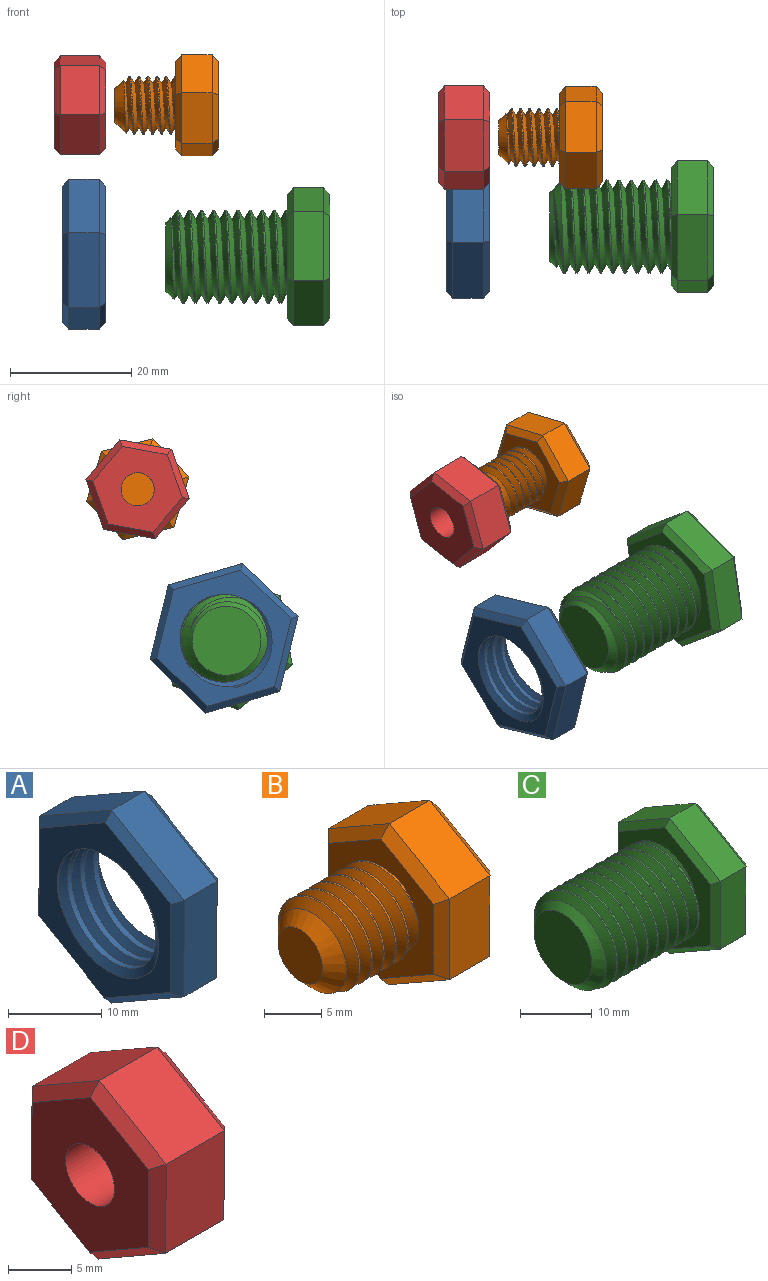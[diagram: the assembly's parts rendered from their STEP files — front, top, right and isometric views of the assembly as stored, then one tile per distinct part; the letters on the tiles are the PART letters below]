
ASSEMBLY  parts=4 mates=2
PART A: 23 faces, bbox 9.3x22.7x26 mm
  f0: cylinder r=7.24mm len=14.48mm, axis (1,0,0), area 111.6mm2, adj f7,f8,f21,f22
  f1: plane 10.98x6.38mm, normal (0,-0.5,0.86), area 63.5mm2, adj f2,f6,f14,f18
  f2: plane 12.7x5mm, normal (0,-1,0), area 63.5mm2, adj f1,f3,f12,f16
  f3: plane 11.02x6.32mm, normal (0,-0.5,-0.87), area 63.5mm2, adj f2,f4,f10,f15
  f4: plane 10.98x6.38mm, normal (0,0.5,-0.86), area 63.5mm2, adj f3,f5,f9,f17
  f5: plane 12.7x5mm, normal (0,1,0), area 63.5mm2, adj f4,f6,f11,f19
  f6: plane 11.02x6.32mm, normal (0,0.5,0.87), area 63.5mm2, adj f1,f5,f13,f20
  f7: plane 23.73x20.67mm, normal (-1,0,0), area 164.4mm2, adj f0,f9,f10,f11,f12,f13,f14,f21
  f8: plane 23.73x20.67mm, normal (1,0,0), area 164.4mm2, adj f0,f15,f16,f17,f18,f19,f20,f21
  f9: plane 10.99x6.96mm, normal (-0.71,0.36,-0.61), area 17.1mm2, adj f4,f7,f10,f11
  f10: plane 11.02x6.9mm, normal (-0.71,-0.35,-0.61), area 17.1mm2, adj f3,f7,f9,f12
  f11: plane 12.7x1.03mm, normal (-0.71,0.71,0), area 17.1mm2, adj f5,f7,f9,f13
  f12: plane 12.7x1.03mm, normal (-0.71,-0.71,0), area 17.1mm2, adj f2,f7,f10,f14
  f13: plane 11.02x6.9mm, normal (-0.71,0.35,0.61), area 17.1mm2, adj f6,f7,f11,f14
  f14: plane 10.99x6.96mm, normal (-0.71,-0.36,0.61), area 17.1mm2, adj f1,f7,f12,f13
  f15: plane 11.02x6.9mm, normal (0.71,-0.35,-0.61), area 17.1mm2, adj f3,f8,f16,f17
  f16: plane 12.7x1.03mm, normal (0.71,-0.71,0), area 17.1mm2, adj f2,f8,f15,f18
  f17: plane 10.99x6.96mm, normal (0.71,0.36,-0.61), area 17.1mm2, adj f4,f8,f15,f19
  f18: plane 10.99x6.96mm, normal (0.71,-0.36,0.61), area 17.1mm2, adj f1,f8,f16,f20
  f19: plane 12.7x1.03mm, normal (0.71,0.71,0), area 17.1mm2, adj f5,f8,f17,f20
  f20: plane 11.02x6.9mm, normal (0.71,0.35,0.61), area 17.1mm2, adj f6,f8,f18,f19
  f21: bspline ~19.31x16.73mm, area 223mm2, adj f0,f7,f8,f22
  f22: bspline ~19.31x16.73mm, area 223mm2, adj f0,f7,f8,f21
PART B: 25 faces, bbox 17.8x15.9x18.1 mm
  f0: cylinder r=4.75mm len=9.5mm, axis (1,0,0), area 28.1mm2, adj f1,f2,f4,f12
  f1: bspline ~10.97x9.91mm, area 196.7mm2, adj f0,f2,f4,f12
  f2: bspline ~10.97x10.66mm, area 196.6mm2, adj f0,f1,f4,f12
  f3: plane 5.5x5.5mm, normal (-1,0,0), area 23.8mm2, adj f4
  f4: cone r=4.75mm half-angle=45deg, axis (1,0,0), area 47.4mm2, adj f0,f1,f2,f3
  f5: plane 7.48x5mm, normal (0,-0.5,0.86), area 43.3mm2, adj f6,f10,f18,f22
  f6: plane 8.66x5mm, normal (0,-1,0), area 43.3mm2, adj f5,f7,f16,f20
  f7: plane 7.52x5mm, normal (0,-0.5,-0.87), area 43.3mm2, adj f6,f8,f14,f19
  f8: plane 7.48x5mm, normal (0,0.5,-0.86), area 43.3mm2, adj f7,f9,f13,f21
  f9: plane 8.66x5mm, normal (0,1,0), area 43.3mm2, adj f8,f10,f15,f23
  f10: plane 7.52x5mm, normal (0,0.5,0.87), area 43.3mm2, adj f5,f9,f17,f24
  f11: plane 15.01x13.03mm, normal (1,0,0), area 146.4mm2, adj f13,f14,f15,f16,f17,f18
  f12: plane 15.83x13.85mm, normal (-1,0,0), area 89.2mm2, adj f0,f1,f2,f19,f20,f21,f22,f23
  f13: plane 7.49x4.93mm, normal (0.71,0.36,-0.61), area 11.4mm2, adj f8,f11,f14,f15
  f14: plane 7.52x4.88mm, normal (0.71,-0.35,-0.61), area 11.4mm2, adj f7,f11,f13,f16
  f15: plane 8.66x1.03mm, normal (0.71,0.71,0), area 11.4mm2, adj f9,f11,f13,f17
  f16: plane 8.66x1.03mm, normal (0.71,-0.71,0), area 11.4mm2, adj f6,f11,f14,f18
  f17: plane 7.52x4.88mm, normal (0.71,0.35,0.61), area 11.4mm2, adj f10,f11,f15,f18
  f18: plane 7.49x4.93mm, normal (0.71,-0.36,0.61), area 11.4mm2, adj f5,f11,f16,f17
  f19: plane 7.52x4.88mm, normal (-0.71,-0.35,-0.61), area 11.4mm2, adj f7,f12,f20,f21
  f20: plane 8.66x1.03mm, normal (-0.71,-0.71,0), area 11.4mm2, adj f6,f12,f19,f22
  f21: plane 7.49x4.93mm, normal (-0.71,0.36,-0.61), area 11.4mm2, adj f8,f12,f19,f23
  f22: plane 7.49x4.93mm, normal (-0.71,-0.36,0.61), area 11.4mm2, adj f5,f12,f20,f24
  f23: plane 8.66x1.03mm, normal (-0.71,0.71,0), area 11.4mm2, adj f9,f12,f21,f24
  f24: plane 7.52x4.88mm, normal (-0.71,0.35,0.61), area 11.4mm2, adj f10,f12,f22,f23
PART C: 26 faces, bbox 27.7x20x23.1 mm
  f0: cylinder r=7.68mm len=18mm, axis (1,0,0), area 139.1mm2, adj f1,f2,f5,f13
  f1: bspline ~20.88x17.74mm, area 713.8mm2, adj f0,f2,f4,f5,f13
  f2: bspline ~21.88x17.74mm, area 715.1mm2, adj f0,f1,f4,f5,f13
  f3: plane 11.36x11.36mm, normal (-1,0,0), area 101.4mm2, adj f4
  f4: cone r=7.68mm half-angle=45deg, axis (1,0,0), area 63.2mm2, adj f1,f2,f3,f5
  f5: cone r=7.68mm half-angle=45deg, axis (1,0,0), area 13.2mm2, adj f0,f1,f2,f4
  f6: plane 9.98x5.81mm, normal (0,-0.5,0.86), area 57.7mm2, adj f7,f11,f19,f23
  f7: plane 11.55x5mm, normal (0,-1,0), area 57.7mm2, adj f6,f8,f17,f21
  f8: plane 10.02x5.74mm, normal (0,-0.5,-0.87), area 57.7mm2, adj f7,f9,f15,f20
  f9: plane 9.98x5.81mm, normal (0,0.5,-0.86), area 57.7mm2, adj f8,f10,f14,f22
  f10: plane 11.55x5mm, normal (0,1,0), area 57.7mm2, adj f9,f11,f16,f24
  f11: plane 10.02x5.74mm, normal (0,0.5,0.87), area 57.7mm2, adj f6,f10,f18,f25
  f12: plane 20.78x18.04mm, normal (1,0,0), area 280.6mm2, adj f14,f15,f16,f17,f18,f19
  f13: plane 20.78x18.04mm, normal (-1,0,0), area 125.2mm2, adj f0,f1,f2,f20,f21,f22,f23,f24
  f14: plane 9.98x6.38mm, normal (0.71,0.36,-0.61), area 15.5mm2, adj f9,f12,f15,f16
  f15: plane 10.02x6.32mm, normal (0.71,-0.35,-0.61), area 15.5mm2, adj f8,f12,f14,f17
  f16: plane 11.55x1.04mm, normal (0.71,0.71,0), area 15.5mm2, adj f10,f12,f14,f18
  f17: plane 11.55x1.04mm, normal (0.71,-0.71,0), area 15.5mm2, adj f7,f12,f15,f19
  f18: plane 10.02x6.32mm, normal (0.71,0.35,0.61), area 15.5mm2, adj f11,f12,f16,f19
  f19: plane 9.98x6.38mm, normal (0.71,-0.36,0.61), area 15.5mm2, adj f6,f12,f17,f18
  f20: plane 10.02x6.32mm, normal (-0.71,-0.35,-0.61), area 15.5mm2, adj f8,f13,f21,f22
  f21: plane 11.55x1.04mm, normal (-0.71,-0.71,0), area 15.5mm2, adj f7,f13,f20,f23
  f22: plane 9.98x6.38mm, normal (-0.71,0.36,-0.61), area 15.5mm2, adj f9,f13,f20,f24
  f23: plane 9.98x6.38mm, normal (-0.71,-0.36,0.61), area 15.5mm2, adj f6,f13,f21,f25
  f24: plane 11.55x1.04mm, normal (-0.71,0.71,0), area 15.5mm2, adj f10,f13,f22,f25
  f25: plane 10.02x6.32mm, normal (-0.71,0.35,0.61), area 15.5mm2, adj f11,f13,f23,f24
PART D: 21 faces, bbox 8.5x15x17.3 mm
  f0: plane 7.49x6.5mm, normal (0,-0.5,0.86), area 56.3mm2, adj f1,f5,f13,f17
  f1: plane 8.66x6.5mm, normal (0,-1,0), area 56.3mm2, adj f0,f2,f11,f15
  f2: plane 7.51x6.5mm, normal (0,-0.5,-0.87), area 56.3mm2, adj f1,f3,f9,f14
  f3: plane 7.49x6.5mm, normal (0,0.5,-0.86), area 56.3mm2, adj f2,f4,f8,f16
  f4: plane 8.66x6.5mm, normal (0,1,0), area 56.3mm2, adj f3,f5,f10,f18
  f5: plane 7.51x6.5mm, normal (0,0.5,0.87), area 56.3mm2, adj f0,f4,f12,f19
  f6: plane 15.01x13.02mm, normal (-1,0,0), area 122.8mm2, adj f8,f9,f10,f11,f12,f13,f20
  f7: plane 15.01x13.02mm, normal (1,0,0), area 122.8mm2, adj f14,f15,f16,f17,f18,f19,f20
  f8: plane 7.49x4.93mm, normal (-0.71,0.36,-0.61), area 11.4mm2, adj f3,f6,f9,f10
  f9: plane 7.51x4.89mm, normal (-0.71,-0.35,-0.61), area 11.4mm2, adj f2,f6,f8,f11
  f10: plane 8.66x1.02mm, normal (-0.71,0.71,0), area 11.4mm2, adj f4,f6,f8,f12
  f11: plane 8.66x1.02mm, normal (-0.71,-0.71,0), area 11.4mm2, adj f1,f6,f9,f13
  f12: plane 7.51x4.89mm, normal (-0.71,0.35,0.61), area 11.4mm2, adj f5,f6,f10,f13
  f13: plane 7.49x4.93mm, normal (-0.71,-0.36,0.61), area 11.4mm2, adj f0,f6,f11,f12
  f14: plane 7.51x4.89mm, normal (0.71,-0.35,-0.61), area 11.4mm2, adj f2,f7,f15,f16
  f15: plane 8.66x1.02mm, normal (0.71,-0.71,0), area 11.4mm2, adj f1,f7,f14,f17
  f16: plane 7.49x4.93mm, normal (0.71,0.36,-0.61), area 11.4mm2, adj f3,f7,f14,f18
  f17: plane 7.49x4.93mm, normal (0.71,-0.36,0.61), area 11.4mm2, adj f0,f7,f15,f19
  f18: plane 8.66x1.02mm, normal (0.71,0.71,0), area 11.4mm2, adj f4,f7,f16,f19
  f19: plane 7.51x4.89mm, normal (0.71,0.35,0.61), area 11.4mm2, adj f5,f7,f17,f18
  f20: cylinder r=2.74mm len=8.5mm, axis (1,0,0), area 146.3mm2, adj f6,f7
PLACE A rot(axis=(0,0.6,-0.8),180deg) t=(-55.27,-6.86,23.48)mm fixed
PLACE B rot(axis=(-1,0,0),43.8deg) t=(-33.16,7.38,48.02)mm
PLACE C rot(axis=(1,0,0),109.9deg) t=(-14.77,-7.25,23.06)mm
PLACE D rot(axis=(1,0,0),100.2deg) t=(-48.16,7.38,48.02)mm fixed
MATE cylindrical C.f0 <-> A.f7  axis (-1,0,0) through (-38.27,-7.25,23.06)mm
MATE cylindrical B.f0 <-> D.f20  axis (-1,0,0) through (-46.66,7.38,48.02)mm
